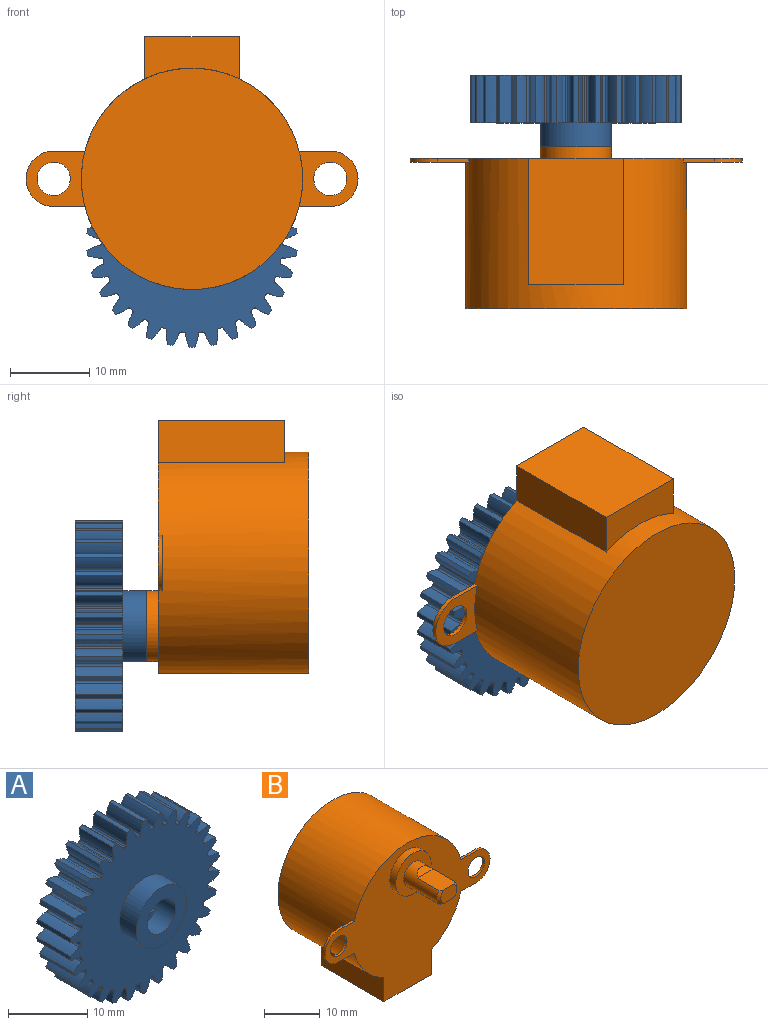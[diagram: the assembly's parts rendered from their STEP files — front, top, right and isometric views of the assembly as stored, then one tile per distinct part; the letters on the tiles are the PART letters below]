
ASSEMBLY  parts=2 mates=1
PART A: 189 faces, bbox 26.6x9x26.7 mm
  f0: plane 4x1mm, normal (0,-1,0), area 2.8mm2, adj f184,f185
  f1: plane 4x1mm, normal (0,-1,0), area 2.8mm2, adj f185,f186
  f2: plane 26.67x26.58mm, normal (0,-1,0), area 421.6mm2, adj f4,f5,f6,f7,f8,f9,f10,f11
  f3: plane 26.67x26.58mm, normal (0,1,0), area 471.2mm2, adj f4,f5,f6,f7,f8,f9,f10,f11
  f4: extruded ~6x1.56mm, area 10.2mm2, adj f2,f3,f123,f124
  f5: cylinder r=11.46mm len=6mm, axis (0,1,0), area 1.8mm2, adj f2,f3,f124,f125
  f6: extruded ~6x1.56mm, area 10.2mm2, adj f2,f3,f7,f125
  f7: cylinder r=13.33mm len=6mm, axis (0,1,0), area 3.7mm2, adj f2,f3,f6,f8
  f8: extruded ~6x1.66mm, area 10.2mm2, adj f2,f3,f7,f126
  f9: cylinder r=11.46mm len=6mm, axis (0,1,0), area 1.8mm2, adj f2,f3,f126,f127
  f10: extruded ~6x1.39mm, area 10.2mm2, adj f2,f3,f11,f127
  f11: cylinder r=13.33mm len=6mm, axis (0,1,0), area 3.7mm2, adj f2,f3,f10,f12
  f12: extruded ~6x1.69mm, area 10.2mm2, adj f2,f3,f11,f128
  f13: cylinder r=11.46mm len=6mm, axis (0,1,0), area 1.8mm2, adj f2,f3,f128,f129
  f14: extruded ~6x1.23mm, area 10.2mm2, adj f2,f3,f15,f129
  f15: cylinder r=13.33mm len=6mm, axis (0,1,0), area 3.7mm2, adj f2,f3,f14,f16
  f16: extruded ~6x1.64mm, area 10.2mm2, adj f2,f3,f15,f130
  f17: cylinder r=11.46mm len=6mm, axis (0,1,0), area 1.8mm2, adj f2,f3,f130,f131
  f18: extruded ~6x1.44mm, area 10.2mm2, adj f2,f3,f19,f131
  f19: cylinder r=13.33mm len=6mm, axis (0,1,0), area 3.7mm2, adj f2,f3,f18,f20
  f20: extruded ~6x1.53mm, area 10.2mm2, adj f2,f3,f19,f132
  f21: cylinder r=11.46mm len=6mm, axis (0,1,0), area 1.8mm2, adj f2,f3,f132,f133
  f22: extruded ~6x1.59mm, area 10.2mm2, adj f2,f3,f23,f133
  f23: cylinder r=13.33mm len=6mm, axis (0,1,0), area 3.7mm2, adj f2,f3,f22,f24
  f24: extruded ~6x1.34mm, area 10.2mm2, adj f2,f3,f23,f134
  f25: cylinder r=11.46mm len=6mm, axis (0,1,0), area 1.8mm2, adj f2,f3,f134,f135
  f26: extruded ~6x1.68mm, area 10.2mm2, adj f2,f3,f27,f135
  f27: cylinder r=13.33mm len=6mm, axis (0,1,0), area 3.7mm2, adj f2,f3,f26,f28
  f28: extruded ~6x1.28mm, area 10.2mm2, adj f2,f3,f27,f136
  f29: cylinder r=11.46mm len=6mm, axis (0,1,0), area 1.8mm2, adj f2,f3,f136,f137
  f30: extruded ~6x1.69mm, area 10.2mm2, adj f2,f3,f31,f137
  f31: cylinder r=13.33mm len=6mm, axis (0,1,0), area 3.7mm2, adj f2,f3,f30,f32
  f32: extruded ~6x1.48mm, area 10.2mm2, adj f2,f3,f31,f138
  f33: cylinder r=11.46mm len=6mm, axis (0,1,0), area 1.8mm2, adj f2,f3,f138,f139
  f34: extruded ~6x1.62mm, area 10.2mm2, adj f2,f3,f35,f139
  f35: cylinder r=13.33mm len=6mm, axis (0,1,0), area 3.7mm2, adj f2,f3,f34,f36
  f36: extruded ~6x1.62mm, area 10.2mm2, adj f2,f3,f35,f140
  f37: cylinder r=11.46mm len=6mm, axis (0,1,0), area 1.8mm2, adj f2,f3,f140,f141
  f38: extruded ~6x1.48mm, area 10.2mm2, adj f2,f3,f39,f141
  f39: cylinder r=13.33mm len=6mm, axis (0,1,0), area 3.7mm2, adj f2,f3,f38,f40
  f40: extruded ~6x1.69mm, area 10.2mm2, adj f2,f3,f39,f142
  f41: cylinder r=11.46mm len=6mm, axis (0,1,0), area 1.8mm2, adj f2,f3,f142,f143
  f42: extruded ~6x1.28mm, area 10.2mm2, adj f2,f3,f43,f143
  f43: cylinder r=13.33mm len=6mm, axis (0,1,0), area 3.7mm2, adj f2,f3,f42,f44
  f44: extruded ~6x1.68mm, area 10.2mm2, adj f2,f3,f43,f144
  f45: cylinder r=11.46mm len=6mm, axis (0,1,0), area 1.8mm2, adj f2,f3,f144,f145
  f46: extruded ~6x1.34mm, area 10.2mm2, adj f2,f3,f47,f145
  f47: cylinder r=13.33mm len=6mm, axis (0,1,0), area 3.7mm2, adj f2,f3,f46,f48
  f48: extruded ~6x1.59mm, area 10.2mm2, adj f2,f3,f47,f146
  f49: cylinder r=11.46mm len=6mm, axis (0,1,0), area 1.8mm2, adj f2,f3,f146,f147
  f50: extruded ~6x1.53mm, area 10.2mm2, adj f2,f3,f51,f147
  f51: cylinder r=13.33mm len=6mm, axis (0,1,0), area 3.7mm2, adj f2,f3,f50,f52
  f52: extruded ~6x1.44mm, area 10.2mm2, adj f2,f3,f51,f148
  f53: cylinder r=11.46mm len=6mm, axis (0,1,0), area 1.8mm2, adj f2,f3,f148,f149
  f54: extruded ~6x1.64mm, area 10.2mm2, adj f2,f3,f55,f149
  f55: cylinder r=13.33mm len=6mm, axis (0,1,0), area 3.7mm2, adj f2,f3,f54,f56
  f56: extruded ~6x1.23mm, area 10.2mm2, adj f2,f3,f55,f150
  f57: cylinder r=11.46mm len=6mm, axis (0,1,0), area 1.8mm2, adj f2,f3,f150,f151
  f58: extruded ~6x1.69mm, area 10.2mm2, adj f2,f3,f59,f151
  f59: cylinder r=13.33mm len=6mm, axis (0,1,0), area 3.7mm2, adj f2,f3,f58,f60
  f60: extruded ~6x1.39mm, area 10.2mm2, adj f2,f3,f59,f152
  f61: cylinder r=11.46mm len=6mm, axis (0,1,0), area 1.8mm2, adj f2,f3,f152,f153
  f62: extruded ~6x1.66mm, area 10.2mm2, adj f2,f3,f63,f153
  f63: cylinder r=13.33mm len=6mm, axis (0,1,0), area 3.7mm2, adj f2,f3,f62,f64
  f64: extruded ~6x1.56mm, area 10.2mm2, adj f2,f3,f63,f154
  f65: cylinder r=11.46mm len=6mm, axis (0,1,0), area 1.8mm2, adj f2,f3,f154,f155
  f66: extruded ~6x1.56mm, area 10.2mm2, adj f2,f3,f67,f155
  f67: cylinder r=13.33mm len=6mm, axis (0,1,0), area 3.7mm2, adj f2,f3,f66,f68
  f68: extruded ~6x1.66mm, area 10.2mm2, adj f2,f3,f67,f156
  f69: cylinder r=11.46mm len=6mm, axis (0,1,0), area 1.8mm2, adj f2,f3,f156,f157
  f70: extruded ~6x1.39mm, area 10.2mm2, adj f2,f3,f71,f157
  f71: cylinder r=13.33mm len=6mm, axis (0,1,0), area 3.7mm2, adj f2,f3,f70,f72
  f72: extruded ~6x1.69mm, area 10.2mm2, adj f2,f3,f71,f158
  f73: cylinder r=11.46mm len=6mm, axis (0,1,0), area 1.8mm2, adj f2,f3,f158,f159
  f74: extruded ~6x1.23mm, area 10.2mm2, adj f2,f3,f75,f159
  f75: cylinder r=13.33mm len=6mm, axis (0,1,0), area 3.7mm2, adj f2,f3,f74,f76
  f76: extruded ~6x1.64mm, area 10.2mm2, adj f2,f3,f75,f160
  f77: cylinder r=11.46mm len=6mm, axis (0,1,0), area 1.8mm2, adj f2,f3,f160,f161
  f78: extruded ~6x1.44mm, area 10.2mm2, adj f2,f3,f79,f161
  f79: cylinder r=13.33mm len=6mm, axis (0,1,0), area 3.7mm2, adj f2,f3,f78,f80
  f80: extruded ~6x1.53mm, area 10.2mm2, adj f2,f3,f79,f162
  f81: cylinder r=11.46mm len=6mm, axis (0,1,0), area 1.8mm2, adj f2,f3,f162,f163
  f82: extruded ~6x1.59mm, area 10.2mm2, adj f2,f3,f83,f163
  f83: cylinder r=13.33mm len=6mm, axis (0,1,0), area 3.7mm2, adj f2,f3,f82,f84
  f84: extruded ~6x1.34mm, area 10.2mm2, adj f2,f3,f83,f164
  f85: cylinder r=11.46mm len=6mm, axis (0,1,0), area 1.8mm2, adj f2,f3,f164,f165
  f86: extruded ~6x1.68mm, area 10.2mm2, adj f2,f3,f87,f165
  f87: cylinder r=13.33mm len=6mm, axis (0,1,0), area 3.7mm2, adj f2,f3,f86,f88
  f88: extruded ~6x1.28mm, area 10.2mm2, adj f2,f3,f87,f166
  f89: cylinder r=11.46mm len=6mm, axis (0,1,0), area 1.8mm2, adj f2,f3,f166,f167
  f90: extruded ~6x1.69mm, area 10.2mm2, adj f2,f3,f91,f167
  f91: cylinder r=13.33mm len=6mm, axis (0,1,0), area 3.7mm2, adj f2,f3,f90,f92
  f92: extruded ~6x1.48mm, area 10.2mm2, adj f2,f3,f91,f168
  f93: cylinder r=11.46mm len=6mm, axis (0,1,0), area 1.8mm2, adj f2,f3,f168,f169
  f94: extruded ~6x1.62mm, area 10.2mm2, adj f2,f3,f95,f169
  f95: cylinder r=13.33mm len=6mm, axis (0,1,0), area 3.7mm2, adj f2,f3,f94,f96
  f96: extruded ~6x1.62mm, area 10.2mm2, adj f2,f3,f95,f170
  f97: cylinder r=11.46mm len=6mm, axis (0,1,0), area 1.8mm2, adj f2,f3,f170,f171
  f98: extruded ~6x1.48mm, area 10.2mm2, adj f2,f3,f99,f171
  f99: cylinder r=13.33mm len=6mm, axis (0,1,0), area 3.7mm2, adj f2,f3,f98,f100
  f100: extruded ~6x1.69mm, area 10.2mm2, adj f2,f3,f99,f172
  f101: cylinder r=11.46mm len=6mm, axis (0,1,0), area 1.8mm2, adj f2,f3,f172,f173
  f102: extruded ~6x1.28mm, area 10.2mm2, adj f2,f3,f103,f173
  f103: cylinder r=13.33mm len=6mm, axis (0,1,0), area 3.7mm2, adj f2,f3,f102,f104
  f104: extruded ~6x1.68mm, area 10.2mm2, adj f2,f3,f103,f174
  f105: cylinder r=11.46mm len=6mm, axis (0,1,0), area 1.8mm2, adj f2,f3,f174,f175
  f106: extruded ~6x1.34mm, area 10.2mm2, adj f2,f3,f107,f175
  f107: cylinder r=13.33mm len=6mm, axis (0,1,0), area 3.7mm2, adj f2,f3,f106,f108
  f108: extruded ~6x1.59mm, area 10.2mm2, adj f2,f3,f107,f176
  f109: cylinder r=11.46mm len=6mm, axis (0,1,0), area 1.8mm2, adj f2,f3,f176,f177
  f110: extruded ~6x1.53mm, area 10.2mm2, adj f2,f3,f111,f177
  f111: cylinder r=13.33mm len=6mm, axis (0,1,0), area 3.7mm2, adj f2,f3,f110,f112
  f112: extruded ~6x1.44mm, area 10.2mm2, adj f2,f3,f111,f178
  f113: cylinder r=11.46mm len=6mm, axis (0,1,0), area 1.8mm2, adj f2,f3,f178,f179
  f114: extruded ~6x1.64mm, area 10.2mm2, adj f2,f3,f115,f179
  f115: cylinder r=13.33mm len=6mm, axis (0,1,0), area 3.7mm2, adj f2,f3,f114,f116
  f116: extruded ~6x1.23mm, area 10.2mm2, adj f2,f3,f115,f180
  f117: cylinder r=11.46mm len=6mm, axis (0,1,0), area 1.8mm2, adj f2,f3,f180,f181
  f118: extruded ~6x1.69mm, area 10.2mm2, adj f2,f3,f119,f181
  f119: cylinder r=13.33mm len=6mm, axis (0,1,0), area 3.7mm2, adj f2,f3,f118,f120
  f120: extruded ~6x1.39mm, area 10.2mm2, adj f2,f3,f119,f182
  f121: cylinder r=11.46mm len=6mm, axis (0,1,0), area 1.8mm2, adj f2,f3,f182,f183
  f122: extruded ~6x1.66mm, area 10.2mm2, adj f2,f3,f123,f183
  f123: cylinder r=13.33mm len=6mm, axis (0,1,0), area 3.7mm2, adj f2,f3,f4,f122
  f124: cylinder r=0.29mm len=6mm, axis (0,1,0), area 2.6mm2, adj f2,f3,f4,f5
  f125: cylinder r=0.29mm len=6mm, axis (0,1,0), area 2.6mm2, adj f2,f3,f5,f6
  f126: cylinder r=0.29mm len=6mm, axis (0,1,0), area 2.6mm2, adj f2,f3,f8,f9
  f127: cylinder r=0.29mm len=6mm, axis (0,1,0), area 2.6mm2, adj f2,f3,f9,f10
  f128: cylinder r=0.29mm len=6mm, axis (0,1,0), area 2.6mm2, adj f2,f3,f12,f13
  f129: cylinder r=0.29mm len=6mm, axis (0,1,0), area 2.6mm2, adj f2,f3,f13,f14
  f130: cylinder r=0.29mm len=6mm, axis (0,1,0), area 2.6mm2, adj f2,f3,f16,f17
  f131: cylinder r=0.29mm len=6mm, axis (0,1,0), area 2.6mm2, adj f2,f3,f17,f18
  f132: cylinder r=0.29mm len=6mm, axis (0,1,0), area 2.6mm2, adj f2,f3,f20,f21
  f133: cylinder r=0.29mm len=6mm, axis (0,1,0), area 2.6mm2, adj f2,f3,f21,f22
  f134: cylinder r=0.29mm len=6mm, axis (0,1,0), area 2.6mm2, adj f2,f3,f24,f25
  f135: cylinder r=0.29mm len=6mm, axis (0,1,0), area 2.6mm2, adj f2,f3,f25,f26
  f136: cylinder r=0.29mm len=6mm, axis (0,1,0), area 2.6mm2, adj f2,f3,f28,f29
  f137: cylinder r=0.29mm len=6mm, axis (0,1,0), area 2.6mm2, adj f2,f3,f29,f30
  f138: cylinder r=0.29mm len=6mm, axis (0,1,0), area 2.6mm2, adj f2,f3,f32,f33
  f139: cylinder r=0.29mm len=6mm, axis (0,1,0), area 2.6mm2, adj f2,f3,f33,f34
  f140: cylinder r=0.29mm len=6mm, axis (0,1,0), area 2.6mm2, adj f2,f3,f36,f37
  f141: cylinder r=0.29mm len=6mm, axis (0,1,0), area 2.6mm2, adj f2,f3,f37,f38
  f142: cylinder r=0.29mm len=6mm, axis (0,1,0), area 2.6mm2, adj f2,f3,f40,f41
  f143: cylinder r=0.29mm len=6mm, axis (0,1,0), area 2.6mm2, adj f2,f3,f41,f42
  f144: cylinder r=0.29mm len=6mm, axis (0,1,0), area 2.6mm2, adj f2,f3,f44,f45
  f145: cylinder r=0.29mm len=6mm, axis (0,1,0), area 2.6mm2, adj f2,f3,f45,f46
  f146: cylinder r=0.29mm len=6mm, axis (0,1,0), area 2.6mm2, adj f2,f3,f48,f49
  f147: cylinder r=0.29mm len=6mm, axis (0,1,0), area 2.6mm2, adj f2,f3,f49,f50
  f148: cylinder r=0.29mm len=6mm, axis (0,1,0), area 2.6mm2, adj f2,f3,f52,f53
  f149: cylinder r=0.29mm len=6mm, axis (0,1,0), area 2.6mm2, adj f2,f3,f53,f54
  f150: cylinder r=0.29mm len=6mm, axis (0,1,0), area 2.6mm2, adj f2,f3,f56,f57
  f151: cylinder r=0.29mm len=6mm, axis (0,1,0), area 2.6mm2, adj f2,f3,f57,f58
  f152: cylinder r=0.29mm len=6mm, axis (0,1,0), area 2.6mm2, adj f2,f3,f60,f61
  f153: cylinder r=0.29mm len=6mm, axis (0,1,0), area 2.6mm2, adj f2,f3,f61,f62
  f154: cylinder r=0.29mm len=6mm, axis (0,1,0), area 2.6mm2, adj f2,f3,f64,f65
  f155: cylinder r=0.29mm len=6mm, axis (0,1,0), area 2.6mm2, adj f2,f3,f65,f66
  f156: cylinder r=0.29mm len=6mm, axis (0,1,0), area 2.6mm2, adj f2,f3,f68,f69
  f157: cylinder r=0.29mm len=6mm, axis (0,1,0), area 2.6mm2, adj f2,f3,f69,f70
  f158: cylinder r=0.29mm len=6mm, axis (0,1,0), area 2.6mm2, adj f2,f3,f72,f73
  f159: cylinder r=0.29mm len=6mm, axis (0,1,0), area 2.6mm2, adj f2,f3,f73,f74
  f160: cylinder r=0.29mm len=6mm, axis (0,1,0), area 2.6mm2, adj f2,f3,f76,f77
  f161: cylinder r=0.29mm len=6mm, axis (0,1,0), area 2.6mm2, adj f2,f3,f77,f78
  f162: cylinder r=0.29mm len=6mm, axis (0,1,0), area 2.6mm2, adj f2,f3,f80,f81
  f163: cylinder r=0.29mm len=6mm, axis (0,1,0), area 2.6mm2, adj f2,f3,f81,f82
  f164: cylinder r=0.29mm len=6mm, axis (0,1,0), area 2.6mm2, adj f2,f3,f84,f85
  f165: cylinder r=0.29mm len=6mm, axis (0,1,0), area 2.6mm2, adj f2,f3,f85,f86
  f166: cylinder r=0.29mm len=6mm, axis (0,1,0), area 2.6mm2, adj f2,f3,f88,f89
  f167: cylinder r=0.29mm len=6mm, axis (0,1,0), area 2.6mm2, adj f2,f3,f89,f90
  f168: cylinder r=0.29mm len=6mm, axis (0,1,0), area 2.6mm2, adj f2,f3,f92,f93
  f169: cylinder r=0.29mm len=6mm, axis (0,1,0), area 2.6mm2, adj f2,f3,f93,f94
  f170: cylinder r=0.29mm len=6mm, axis (0,1,0), area 2.6mm2, adj f2,f3,f96,f97
  f171: cylinder r=0.29mm len=6mm, axis (0,1,0), area 2.6mm2, adj f2,f3,f97,f98
  f172: cylinder r=0.29mm len=6mm, axis (0,1,0), area 2.6mm2, adj f2,f3,f100,f101
  f173: cylinder r=0.29mm len=6mm, axis (0,1,0), area 2.6mm2, adj f2,f3,f101,f102
  f174: cylinder r=0.29mm len=6mm, axis (0,1,0), area 2.6mm2, adj f2,f3,f104,f105
  f175: cylinder r=0.29mm len=6mm, axis (0,1,0), area 2.6mm2, adj f2,f3,f105,f106
  f176: cylinder r=0.29mm len=6mm, axis (0,1,0), area 2.6mm2, adj f2,f3,f108,f109
  f177: cylinder r=0.29mm len=6mm, axis (0,1,0), area 2.6mm2, adj f2,f3,f109,f110
  f178: cylinder r=0.29mm len=6mm, axis (0,1,0), area 2.6mm2, adj f2,f3,f112,f113
  f179: cylinder r=0.29mm len=6mm, axis (0,1,0), area 2.6mm2, adj f2,f3,f113,f114
  f180: cylinder r=0.29mm len=6mm, axis (0,1,0), area 2.6mm2, adj f2,f3,f116,f117
  f181: cylinder r=0.29mm len=6mm, axis (0,1,0), area 2.6mm2, adj f2,f3,f117,f118
  f182: cylinder r=0.29mm len=6mm, axis (0,1,0), area 2.6mm2, adj f2,f3,f120,f121
  f183: cylinder r=0.29mm len=6mm, axis (0,1,0), area 2.6mm2, adj f2,f3,f121,f122
  f184: plane 6x4mm, normal (0,0,-1), area 24mm2, adj f0,f3,f185
  f185: cylinder r=2.5mm len=9mm, axis (0,-1,0), area 85.7mm2, adj f0,f1,f3,f184,f186,f188
  f186: plane 6x4mm, normal (0,0,1), area 24mm2, adj f1,f3,f185
  f187: cylinder r=4.5mm len=9mm, axis (0,1,0), area 84.8mm2, adj f2,f188
  f188: plane 9x9mm, normal (0,-1,0), area 44mm2, adj f185,f187
PART B: 27 faces, bbox 42x29.5x32 mm
  f0: cylinder r=14mm len=28mm, axis (0,-1,0), area 1465.8mm2, adj f1,f2,f3,f5,f6,f7,f10,f11
  f1: plane 28x28mm, normal (0,1,0), area 615.8mm2, adj f0
  f2: plane 42x32mm, normal (0,-1,0), area 667.3mm2, adj f0,f3,f4,f5,f7,f8,f9,f10
  f3: plane 16x5.35mm, normal (-1,0,0), area 85.6mm2, adj f0,f2,f4,f6
  f4: plane 16x12mm, normal (0,0,-1), area 192mm2, adj f2,f3,f5,f6
  f5: plane 16x5.35mm, normal (1,0,0), area 85.6mm2, adj f0,f2,f4,f6
  f6: plane 12x5.35mm, normal (0,1,0), area 53.3mm2, adj f0,f3,f4,f5
  f7: plane 3.94x0.5mm, normal (0,0,1), area 2mm2, adj f0,f2,f8,f11
  f8: cylinder r=3.5mm len=7mm, axis (0,-1,0), area 5.5mm2, adj f2,f7,f10,f11
  f9: cylinder r=2.1mm len=4.2mm, axis (0,-1,0), area 6.6mm2, adj f2,f11
  f10: plane 3.94x0.5mm, normal (0,0,-1), area 2mm2, adj f0,f2,f8,f11
  f11: plane 7.44x7mm, normal (0,1,0), area 30.9mm2, adj f0,f7,f8,f9,f10
  f12: plane 3.94x0.5mm, normal (0,0,1), area 2mm2, adj f0,f2,f14,f16
  f13: plane 3.94x0.5mm, normal (0,0,-1), area 2mm2, adj f0,f2,f14,f16
  f14: cylinder r=3.5mm len=7mm, axis (0,-1,0), area 5.5mm2, adj f2,f12,f13,f16
  f15: cylinder r=2.1mm len=4.2mm, axis (0,-1,0), area 6.6mm2, adj f2,f16
  f16: plane 7.44x7mm, normal (0,1,0), area 30.9mm2, adj f0,f12,f13,f14,f15
  f17: cylinder r=4.5mm len=9mm, axis (0,1,0), area 42.4mm2, adj f2,f18
  f18: plane 9x9mm, normal (0,-1,0), area 44mm2, adj f17,f19
  f19: cylinder r=2.5mm len=8.5mm, axis (0,1,0), area 76.4mm2, adj f18,f21,f22,f23,f24,f25,f26
  f20: plane 4x3mm, normal (0,-1,0), area 10.8mm2, adj f21,f22,f25,f26
  f21: plane 6x4mm, normal (0,0,-1), area 23.7mm2, adj f19,f20,f23,f25,f26
  f22: plane 6x4mm, normal (0,0,1), area 23.7mm2, adj f19,f20,f24,f25,f26
  f23: plane 4x1mm, normal (0,-0.71,-0.71), area 4mm2, adj f19,f21
  f24: plane 4x1mm, normal (0,-0.71,0.71), area 4mm2, adj f19,f22
  f25: cone r=2mm half-angle=45deg, axis (0,1,0), area 2.3mm2, adj f19,f20,f21,f22
  f26: cone r=2mm half-angle=45deg, axis (0,1,0), area 2.3mm2, adj f19,f20,f21,f22
PLACE A t=(46.04,-17.05,-22.78)mm
PLACE B rot(axis=(-1,0,0),180deg) t=(46.04,-27.55,-14.78)mm
MATE slider A.f185 <-> B.f17  axis (0,-1,0) through (46.04,-26.05,-22.78)mm
